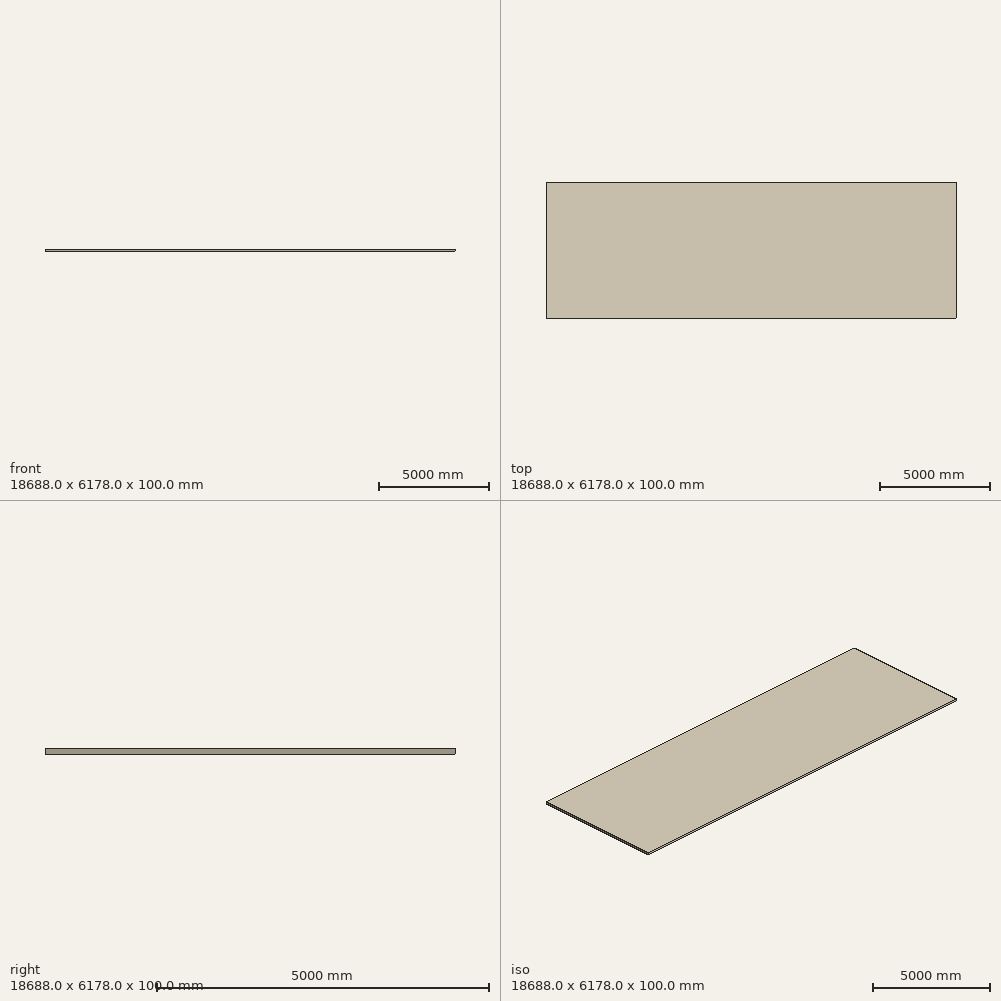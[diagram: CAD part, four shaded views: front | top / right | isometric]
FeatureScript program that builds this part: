
annotation { "Feature Type Name" : "Feature", "Feature Type Description" : "" }
export const myFeature = defineFeature(function(context is Context, id is Id, definition is map)
    precondition{}
    {
        {
            var Q0;
            Q0=qCreatedBy(makeId("Top.planeOp"),FACE);
            var sketch = newSketch(context, id + "F0", { "sketchPlane" : qUnion([Q0])});
            skLineSegment(sketch, "E0.bottom", {"start": v(0, 0) * mm, "end": v(18688, 0) * mm});
            skLineSegment(sketch, "E0.top", {"start": v(0, 6178) * mm, "end": v(18688, 6178) * mm});
            skLineSegment(sketch, "E0.left", {"start": v(0, 0) * mm, "end": v(0, 6178) * mm});
            skLineSegment(sketch, "E0.right", {"start": v(18688, 0) * mm, "end": v(18688, 6178) * mm});
            skSolve(sketch);
        }
        {
            var Q0;
            Q0=makeQuery(id+"F0.imprint","IMPRINT",FACE,{"disambiguationData":[TD([[makeQuery(id+"F0.imprint","IMPRINT",EDGE,{"derivedFrom":sQuery(id+"F0.wireOp",EDGE,"E0.bottom")}),1.0]])]});
            extrude(context, id + "F1", {"entities" : qUnion([Q0]), "oppositeDirection" : true, "depth" : 100 * mm});
        }
    });
